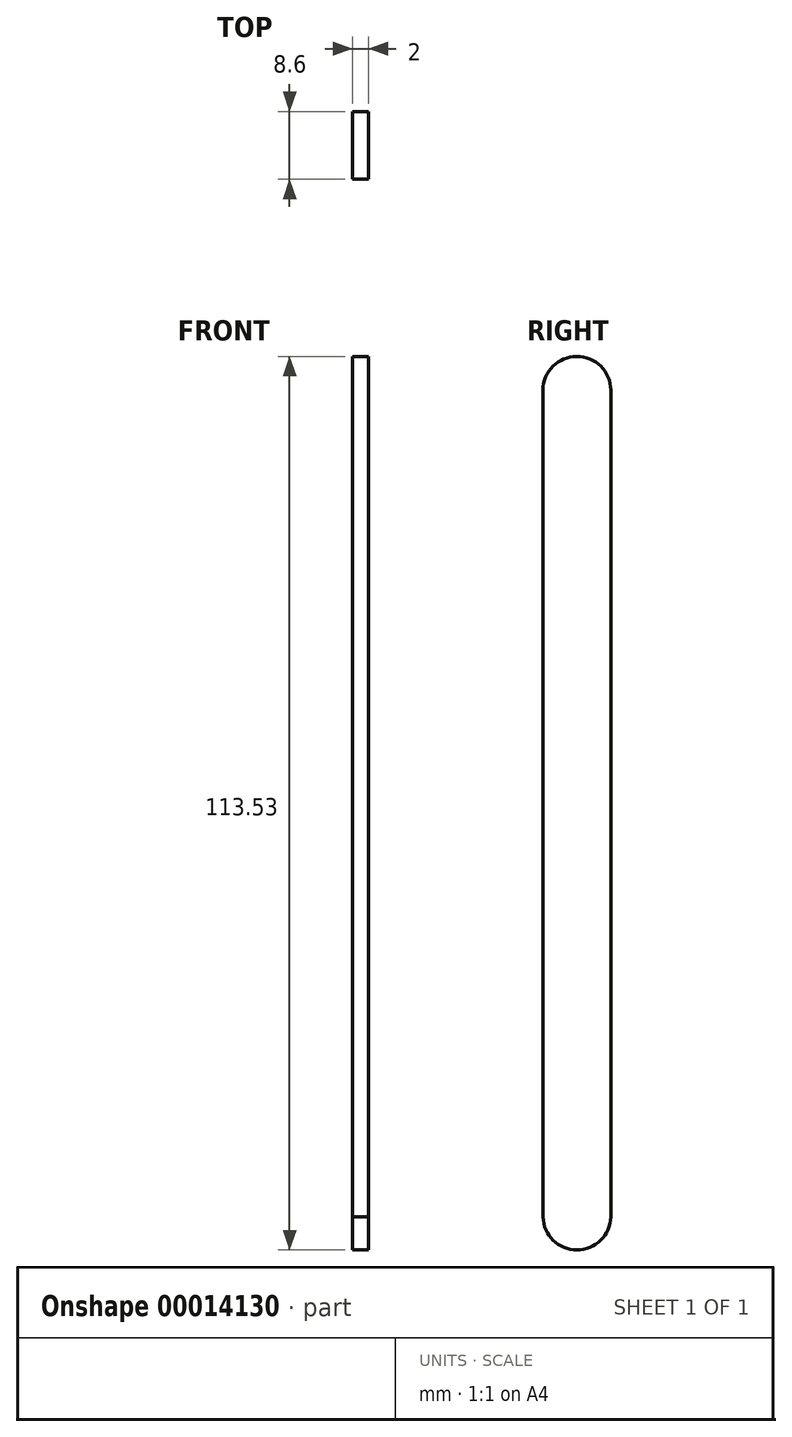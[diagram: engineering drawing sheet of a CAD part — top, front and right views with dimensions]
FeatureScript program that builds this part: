
annotation { "Feature Type Name" : "Feature", "Feature Type Description" : "" }
export const myFeature = defineFeature(function(context is Context, id is Id, definition is map)
    precondition{}
    {
        {
            var Q0;
            Q0=qCreatedBy(makeId("Right.planeOp"),FACE);
            var sketch = newSketch(context, id + "F0", { "sketchPlane" : qUnion([Q0])});
            skLineSegment(sketch, "E0", {"start": v(-8.6, 50.69) * mm, "end": v(-8.6, -54.31) * mm});
            skLineSegment(sketch, "E1", {"start": v(0, 50.69) * mm, "end": v(0, -54.31) * mm});
            skArc(sketch, "E2", {"start": v(0, 50.69) * mm, "mid": v(-4.3, 54.99) * mm, "end": v(-8.6, 50.69) * mm});
            skArc(sketch, "E3", {"start": v(-8.6, -54.31) * mm, "mid": v(-4.3, -58.54) * mm, "end": v(0, -54.31) * mm});
            skSolve(sketch);
        }
        {
            var Q0;
            Q0=makeQuery(id+"F0.imprint","IMPRINT",FACE,{"disambiguationData":[TD([[makeQuery(id+"F0.imprint","IMPRINT",EDGE,{"derivedFrom":sQuery(id+"F0.wireOp",EDGE,"E0")}),1.0]])]});
            extrude(context, id + "F1", {"entities" : qUnion([Q0]), "depth" : 2 * mm});
        }
    });
